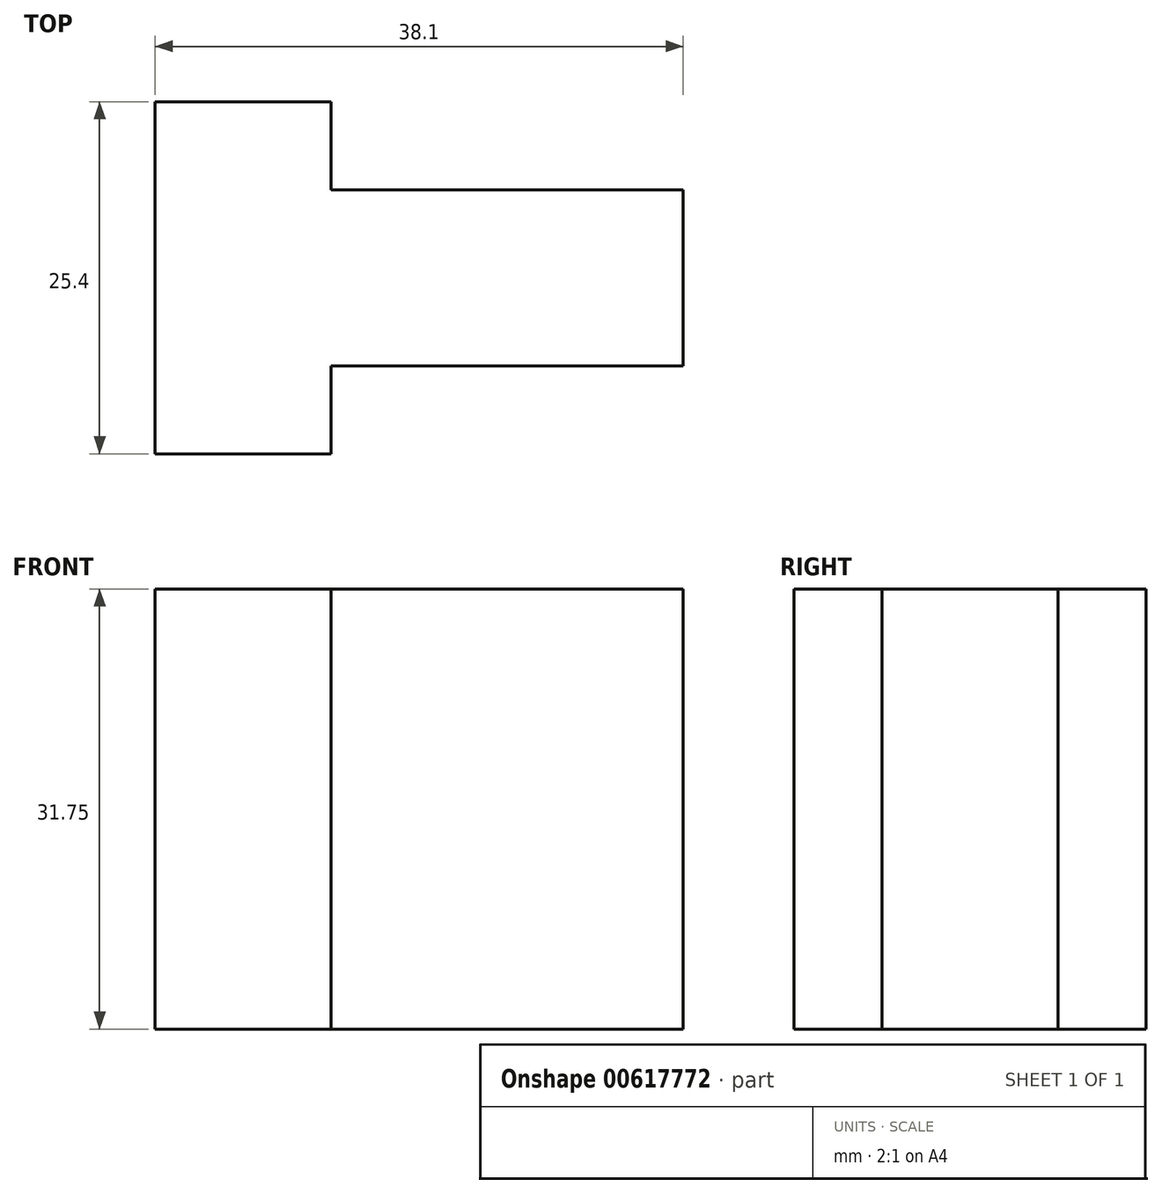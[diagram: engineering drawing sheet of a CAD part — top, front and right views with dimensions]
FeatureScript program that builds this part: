
annotation { "Feature Type Name" : "Feature", "Feature Type Description" : "" }
export const myFeature = defineFeature(function(context is Context, id is Id, definition is map)
    precondition{}
    {
        {
            var Q0;
            Q0=qCreatedBy(makeId("Top.planeOp"),FACE);
            var sketch = newSketch(context, id + "F0", { "sketchPlane" : qUnion([Q0])});
            skLineSegment(sketch, "E0", {"start": v(0, 25.4) * mm, "end": v(0, 0) * mm});
            skLineSegment(sketch, "E1", {"start": v(0, 0) * mm, "end": v(12.7, 0) * mm});
            skLineSegment(sketch, "E2", {"start": v(12.7, 0) * mm, "end": v(12.7, 6.35) * mm});
            skLineSegment(sketch, "E3", {"start": v(12.7, 6.35) * mm, "end": v(38.1, 6.35) * mm});
            skLineSegment(sketch, "E4", {"start": v(38.1, 6.35) * mm, "end": v(38.1, 19.05) * mm});
            skLineSegment(sketch, "E5", {"start": v(38.1, 19.05) * mm, "end": v(12.7, 19.05) * mm});
            skLineSegment(sketch, "E6", {"start": v(12.7, 19.05) * mm, "end": v(12.7, 25.4) * mm});
            skLineSegment(sketch, "E7", {"start": v(12.7, 25.4) * mm, "end": v(0, 25.4) * mm});
            skSolve(sketch);
        }
        {
            var Q0;
            Q0=makeQuery(id+"F0.imprint","IMPRINT",FACE,{"disambiguationData":[TD([[makeQuery(id+"F0.imprint","IMPRINT",EDGE,{"derivedFrom":sQuery(id+"F0.wireOp",EDGE,"E0")}),1.0]])]});
            extrude(context, id + "F1", {"entities" : qUnion([Q0]), "depth" : 31.75 * mm, "offsetDistance" : 25.4 * mm});
        }
    });
